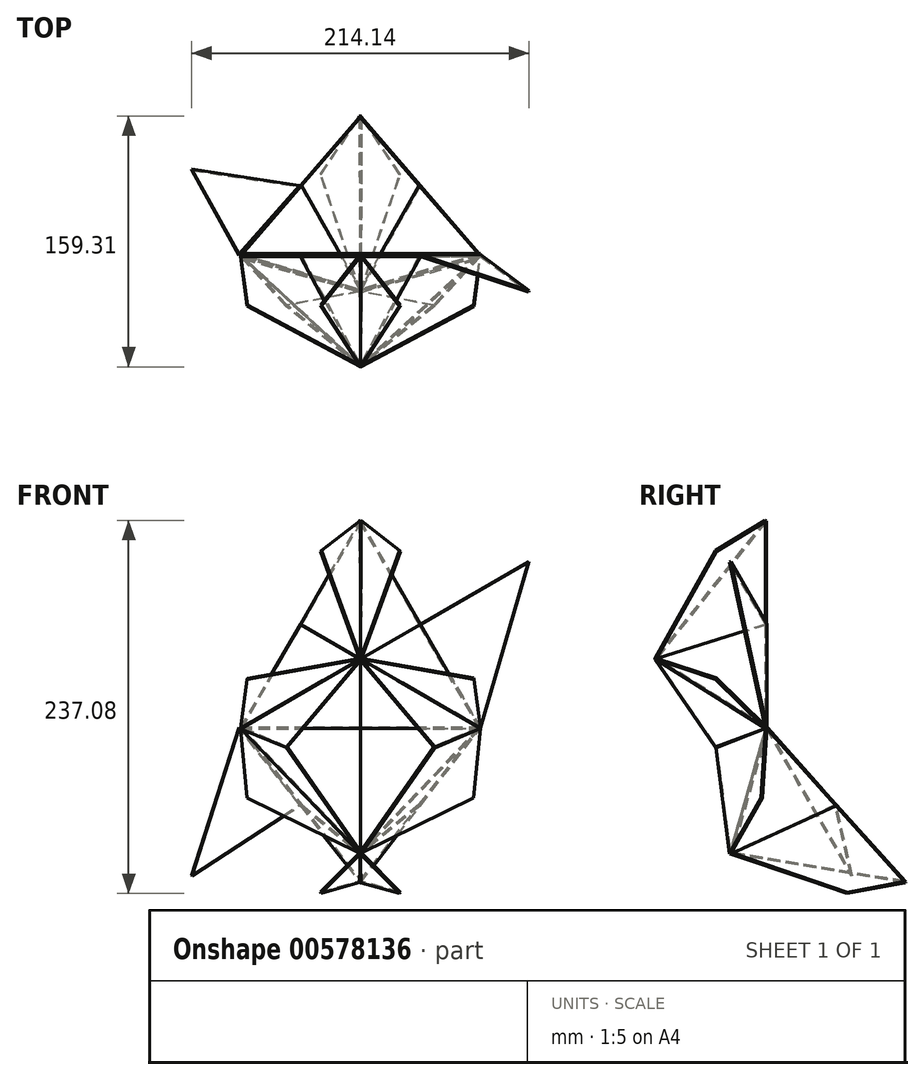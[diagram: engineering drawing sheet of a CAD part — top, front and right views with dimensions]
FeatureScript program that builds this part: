
annotation { "Feature Type Name" : "Feature", "Feature Type Description" : "" }
export const myFeature = defineFeature(function(context is Context, id is Id, definition is map)
    precondition{}
    {
        {
            var Q0;
            Q0=qCreatedBy(makeId("Front.planeOp"),FACE);
            var sketch = newSketch(context, id + "F0", { "sketchPlane" : qUnion([Q0])});
            skLineSegment(sketch, "E0", {"start": v(0, 0) * mm, "end": v(76.2, 0) * mm});
            skLineSegment(sketch, "E1", {"start": v(76.2, 0) * mm, "end": v(152.4, 0) * mm});
            skLineSegment(sketch, "E2", {"start": v(76.2, 0) * mm, "end": v(76.2, -82.55) * mm});
            skLineSegment(sketch, "E3", {"start": v(0, 0) * mm, "end": v(38.1, 66) * mm});
            skLineSegment(sketch, "E4", {"start": v(38.1, 66) * mm, "end": v(76.2, 131.98) * mm});
            skLineSegment(sketch, "E5", {"start": v(76.2, 131.98) * mm, "end": v(114.3, 66) * mm});
            skLineSegment(sketch, "E6", {"start": v(114.3, 66) * mm, "end": v(152.4, 0) * mm});
            skLineSegment(sketch, "E7", {"start": v(38.1, 66) * mm, "end": v(-33.4, 107.27) * mm});
            skLineSegment(sketch, "E8", {"start": v(114.3, 66) * mm, "end": v(185.8, 107.27) * mm});
            skLineSegment(sketch, "E9", {"start": v(0, 0) * mm, "end": v(76.2, -82.55) * mm});
            skLineSegment(sketch, "E10", {"start": v(152.4, 0) * mm, "end": v(76.2, -82.55) * mm});
            skLineSegment(sketch, "E11", {"start": v(76.2, 131.98) * mm, "end": v(185.8, 107.27) * mm});
            skLineSegment(sketch, "E12", {"start": v(152.4, 0) * mm, "end": v(185.8, 107.27) * mm});
            skLineSegment(sketch, "E13", {"start": v(76.2, 131.98) * mm, "end": v(-33.4, 107.27) * mm});
            skLineSegment(sketch, "E14", {"start": v(-33.4, 107.27) * mm, "end": v(0, 0) * mm});
            skLineSegment(sketch, "E15", {"start": v(76.2, -82.55) * mm, "end": v(3.02, -44.35) * mm});
            skLineSegment(sketch, "E16", {"start": v(3.02, -44.35) * mm, "end": v(0, 0) * mm});
            skLineSegment(sketch, "E17", {"start": v(76.2, -82.55) * mm, "end": v(149.38, -44.35) * mm});
            skLineSegment(sketch, "E18", {"start": v(149.38, -44.35) * mm, "end": v(152.4, 0) * mm});
            skLineSegment(sketch, "E19", {"start": v(152.4, 0) * mm, "end": v(189.3, 24.8) * mm});
            skLineSegment(sketch, "E20", {"start": v(189.3, 24.8) * mm, "end": v(185.8, 107.27) * mm});
            skLineSegment(sketch, "E21", {"start": v(185.8, 107.27) * mm, "end": v(116.12, 151.54) * mm});
            skLineSegment(sketch, "E22", {"start": v(116.12, 151.54) * mm, "end": v(76.2, 131.98) * mm});
            skLineSegment(sketch, "E23", {"start": v(-33.4, 107.27) * mm, "end": v(36.28, 151.54) * mm});
            skLineSegment(sketch, "E24", {"start": v(36.28, 151.54) * mm, "end": v(76.2, 131.98) * mm});
            skLineSegment(sketch, "E25", {"start": v(-33.4, 107.27) * mm, "end": v(-36.9, 24.8) * mm});
            skLineSegment(sketch, "E26", {"start": v(-36.9, 24.8) * mm, "end": v(0, 0) * mm});
            skLineSegment(sketch, "E27", {"start": v(-36.9, 24.8) * mm, "end": v(-65.66, 38.24) * mm});
            skLineSegment(sketch, "E28", {"start": v(-65.66, 38.24) * mm, "end": v(-33.4, 107.27) * mm});
            skLineSegment(sketch, "E29", {"start": v(36.28, 151.54) * mm, "end": v(10.26, 169.73) * mm});
            skLineSegment(sketch, "E30", {"start": v(10.26, 169.73) * mm, "end": v(-33.4, 107.27) * mm});
            skLineSegment(sketch, "E31", {"start": v(3.02, -44.35) * mm, "end": v(0.28, -75.98) * mm});
            skLineSegment(sketch, "E32", {"start": v(0.28, -75.98) * mm, "end": v(76.2, -82.55) * mm});
            skLineSegment(sketch, "E33", {"start": v(149.38, -44.35) * mm, "end": v(152.12, -75.98) * mm});
            skLineSegment(sketch, "E34", {"start": v(152.12, -75.98) * mm, "end": v(76.2, -82.55) * mm});
            skLineSegment(sketch, "E35", {"start": v(189.3, 24.8) * mm, "end": v(218.06, 38.24) * mm});
            skLineSegment(sketch, "E36", {"start": v(218.06, 38.24) * mm, "end": v(185.8, 107.27) * mm});
            skLineSegment(sketch, "E37", {"start": v(116.12, 151.54) * mm, "end": v(142.14, 169.73) * mm});
            skLineSegment(sketch, "E38", {"start": v(142.14, 169.73) * mm, "end": v(185.8, 107.27) * mm});
            skSolve(sketch);
        }
        {
            var Q0;
            Q0=makeQuery(id+"F0.imprint","IMPRINT",FACE,{"disambiguationData":[TD([[makeQuery(id+"F0.imprint","IMPRINT",EDGE,{"derivedFrom":sQuery(id+"F0.wireOp",EDGE,"E4")}),1.0]])]});
            var Q1;
            Q1=makeQuery(id+"F0.imprint","IMPRINT",FACE,{"disambiguationData":[TD([[makeQuery(id+"F0.imprint","IMPRINT",EDGE,{"derivedFrom":sQuery(id+"F0.wireOp",EDGE,"E0")}),-1.0]])]});
            var Q2;
            Q2=makeQuery(id+"F0.imprint","IMPRINT",FACE,{"disambiguationData":[TD([[makeQuery(id+"F0.imprint","IMPRINT",EDGE,{"derivedFrom":sQuery(id+"F0.wireOp",EDGE,"E6")}),1.0]])]});
            extrude(context, id + "F1", {"entities" : qUnion([Q0, Q1, Q2]), "depth" : 1.02 * mm, "offsetDistance" : 25.4 * mm});
        }
        {
            var Q0;
            Q0=makeQuery(id+"F1.opExtrude","SWEPT_BODY",BODY,{"disambiguationData":[OSD([sQuery(id+"F0.wireOp",EDGE,"E3"),sQuery(id+"F0.wireOp",EDGE,"E4"),sQuery(id+"F0.wireOp",EDGE,"E13"),sQuery(id+"F0.wireOp",EDGE,"E14")])]});
            var Q1;
            Q1=makeQuery(id+"F1.opExtrude","CAP_EDGE",EDGE,{"disambiguationData":[OSD([sQuery(id+"F0.wireOp",EDGE,"E3"),sQuery(id+"F0.wireOp",EDGE,"E4")])],"isStart":true});
            transform(context, id + "F2", {"entities" : qUnion([Q0]), "transformType" : TransformType.ROTATION, "transformAxis" : qUnion([Q1]), "angle" : 122 * degree, "makeCopy" : false});
        }
        {
            var Q0;
            Q0=makeQuery(id+"F1.opExtrude","SWEPT_BODY",BODY,{"disambiguationData":[OSD([sQuery(id+"F0.wireOp",EDGE,"E0"),sQuery(id+"F0.wireOp",EDGE,"E1"),sQuery(id+"F0.wireOp",EDGE,"E9"),sQuery(id+"F0.wireOp",EDGE,"E10")])]});
            var Q1;
            Q1=makeQuery(id+"F1.opExtrude","CAP_EDGE",EDGE,{"disambiguationData":[OSD([sQuery(id+"F0.wireOp",EDGE,"E0"),sQuery(id+"F0.wireOp",EDGE,"E1")])],"isStart":true});
            transform(context, id + "F3", {"entities" : qUnion([Q0]), "transformType" : TransformType.ROTATION, "transformAxis" : qUnion([Q1]), "angle" : 122 * degree, "oppositeDirection" : true, "makeCopy" : false});
        }
        {
            var Q0;
            Q0=makeQuery(id+"F1.opExtrude","SWEPT_BODY",BODY,{"disambiguationData":[OSD([sQuery(id+"F0.wireOp",EDGE,"E5"),sQuery(id+"F0.wireOp",EDGE,"E6"),sQuery(id+"F0.wireOp",EDGE,"E11"),sQuery(id+"F0.wireOp",EDGE,"E12")])]});
            var Q1;
            Q1=makeQuery(id+"F1.opExtrude","CAP_EDGE",EDGE,{"disambiguationData":[OSD([sQuery(id+"F0.wireOp",EDGE,"E5"),sQuery(id+"F0.wireOp",EDGE,"E6")])],"isStart":true});
            transform(context, id + "F4", {"entities" : qUnion([Q0]), "transformType" : TransformType.ROTATION, "transformAxis" : qUnion([Q1]), "angle" : 122 * degree, "makeCopy" : false});
        }
        {
            var Q0;
            Q0=makeQuery(id+"F0.imprint","IMPRINT",FACE,{"disambiguationData":[TD([[makeQuery(id+"F0.imprint","IMPRINT",EDGE,{"derivedFrom":sQuery(id+"F0.wireOp",EDGE,"E3")}),1.0]])]});
            var Q1;
            Q1=makeQuery(id+"F0.imprint","IMPRINT",FACE,{"disambiguationData":[TD([[makeQuery(id+"F0.imprint","IMPRINT",EDGE,{"derivedFrom":sQuery(id+"F0.wireOp",EDGE,"E1")}),-1.0]])]});
            var Q2;
            Q2=makeQuery(id+"F0.imprint","IMPRINT",FACE,{"disambiguationData":[TD([[makeQuery(id+"F0.imprint","IMPRINT",EDGE,{"derivedFrom":sQuery(id+"F0.wireOp",EDGE,"E5")}),1.0]])]});
            extrude(context, id + "F5", {"entities" : qUnion([Q0, Q1, Q2]), "depth" : 1.02 * mm, "offsetDistance" : 25.4 * mm});
        }
        {
            var Q0;
            Q0=makeQuery(id+"F5.opExtrude","SWEPT_BODY",BODY,{"disambiguationData":[OSD([sQuery(id+"F0.wireOp",EDGE,"E3"),sQuery(id+"F0.wireOp",EDGE,"E7"),sQuery(id+"F0.wireOp",EDGE,"E14")])]});
            var Q1;
            Q1=sQuery(id+"F0.wireOp",EDGE,"E3");
            transform(context, id + "F6", {"entities" : qUnion([Q0]), "transformType" : TransformType.ROTATION, "transformAxis" : qUnion([Q1]), "angle" : 122 * degree, "makeCopy" : false});
        }
        {
            var Q0;
            Q0=makeQuery(id+"F5.opExtrude","SWEPT_BODY",BODY,{"disambiguationData":[OSD([sQuery(id+"F0.wireOp",EDGE,"E1"),sQuery(id+"F0.wireOp",EDGE,"E2"),sQuery(id+"F0.wireOp",EDGE,"E10")])]});
            var Q1;
            Q1=sQuery(id+"F0.wireOp",EDGE,"E1");
            transform(context, id + "F7", {"entities" : qUnion([Q0]), "transformType" : TransformType.ROTATION, "transformAxis" : qUnion([Q1]), "angle" : 122 * degree, "oppositeDirection" : true, "makeCopy" : false});
        }
        {
            var Q0;
            Q0=makeQuery(id+"F5.opExtrude","SWEPT_BODY",BODY,{"disambiguationData":[OSD([sQuery(id+"F0.wireOp",EDGE,"E5"),sQuery(id+"F0.wireOp",EDGE,"E8"),sQuery(id+"F0.wireOp",EDGE,"E11")])]});
            var Q1;
            Q1=sQuery(id+"F0.wireOp",EDGE,"E5");
            transform(context, id + "F8", {"entities" : qUnion([Q0]), "transformType" : TransformType.ROTATION, "transformAxis" : qUnion([Q1]), "angle" : 122 * degree, "makeCopy" : false});
        }
        {
            var Q0;
            Q0=makeQuery(id+"F0.imprint","IMPRINT",FACE,{"disambiguationData":[TD([[makeQuery(id+"F0.imprint","IMPRINT",EDGE,{"derivedFrom":sQuery(id+"F0.wireOp",EDGE,"E13")}),-1.0]])]});
            var Q1;
            Q1=makeQuery(id+"F0.imprint","IMPRINT",FACE,{"disambiguationData":[TD([[makeQuery(id+"F0.imprint","IMPRINT",EDGE,{"derivedFrom":sQuery(id+"F0.wireOp",EDGE,"E14")}),-1.0]])]});
            var Q2;
            Q2=makeQuery(id+"F0.imprint","IMPRINT",FACE,{"disambiguationData":[TD([[makeQuery(id+"F0.imprint","IMPRINT",EDGE,{"derivedFrom":sQuery(id+"F0.wireOp",EDGE,"E11")}),1.0]])]});
            var Q3;
            Q3=makeQuery(id+"F0.imprint","IMPRINT",FACE,{"disambiguationData":[TD([[makeQuery(id+"F0.imprint","IMPRINT",EDGE,{"derivedFrom":sQuery(id+"F0.wireOp",EDGE,"E12")}),-1.0]])]});
            var Q4;
            Q4=makeQuery(id+"F0.imprint","IMPRINT",FACE,{"disambiguationData":[TD([[makeQuery(id+"F0.imprint","IMPRINT",EDGE,{"derivedFrom":sQuery(id+"F0.wireOp",EDGE,"E10")}),1.0]])]});
            var Q5;
            Q5=makeQuery(id+"F0.imprint","IMPRINT",FACE,{"disambiguationData":[TD([[makeQuery(id+"F0.imprint","IMPRINT",EDGE,{"derivedFrom":sQuery(id+"F0.wireOp",EDGE,"E9")}),-1.0]])]});
            extrude(context, id + "F9", {"entities" : qUnion([Q0, Q1, Q2, Q3, Q4, Q5]), "depth" : 1.02 * mm, "offsetDistance" : 25.4 * mm});
        }
        {
            var Q0;
            Q0=makeQuery(id+"F9.opExtrude","SWEPT_BODY",BODY,{"disambiguationData":[OSD([sQuery(id+"F0.wireOp",EDGE,"E14"),sQuery(id+"F0.wireOp",EDGE,"E25"),sQuery(id+"F0.wireOp",EDGE,"E26")])]});
            var Q1;
            Q1=makeQuery(id+"F9.opExtrude","SWEPT_BODY",BODY,{"disambiguationData":[OSD([sQuery(id+"F0.wireOp",EDGE,"E13"),sQuery(id+"F0.wireOp",EDGE,"E23"),sQuery(id+"F0.wireOp",EDGE,"E24")])]});
            var Q2;
            Q2=sQuery(id+"F0.wireOp",EDGE,"E3");
            transform(context, id + "F10", {"entities" : qUnion([Q0, Q1]), "transformType" : TransformType.ROTATION, "transformAxis" : qUnion([Q2]), "angle" : 122 * degree, "makeCopy" : false});
        }
        {
            var Q0;
            Q0=makeQuery(id+"F9.opExtrude","SWEPT_BODY",BODY,{"disambiguationData":[OSD([sQuery(id+"F0.wireOp",EDGE,"E9"),sQuery(id+"F0.wireOp",EDGE,"E15"),sQuery(id+"F0.wireOp",EDGE,"E16")])]});
            var Q1;
            Q1=makeQuery(id+"F9.opExtrude","SWEPT_BODY",BODY,{"disambiguationData":[OSD([sQuery(id+"F0.wireOp",EDGE,"E10"),sQuery(id+"F0.wireOp",EDGE,"E17"),sQuery(id+"F0.wireOp",EDGE,"E18")])]});
            var Q2;
            Q2=sQuery(id+"F0.wireOp",EDGE,"E1");
            transform(context, id + "F11", {"entities" : qUnion([Q0, Q1]), "transformType" : TransformType.ROTATION, "transformAxis" : qUnion([Q2]), "angle" : 122 * degree, "oppositeDirection" : true, "makeCopy" : false});
        }
        {
            var Q0;
            Q0=makeQuery(id+"F9.opExtrude","SWEPT_BODY",BODY,{"disambiguationData":[OSD([sQuery(id+"F0.wireOp",EDGE,"E12"),sQuery(id+"F0.wireOp",EDGE,"E19"),sQuery(id+"F0.wireOp",EDGE,"E20")])]});
            var Q1;
            Q1=makeQuery(id+"F9.opExtrude","SWEPT_BODY",BODY,{"disambiguationData":[OSD([sQuery(id+"F0.wireOp",EDGE,"E11"),sQuery(id+"F0.wireOp",EDGE,"E21"),sQuery(id+"F0.wireOp",EDGE,"E22")])]});
            var Q2;
            Q2=sQuery(id+"F0.wireOp",EDGE,"E6");
            transform(context, id + "F12", {"entities" : qUnion([Q0, Q1]), "transformType" : TransformType.ROTATION, "transformAxis" : qUnion([Q2]), "angle" : 122 * degree, "makeCopy" : false});
        }
        {
            var Q0;
            Q0=makeQuery(id+"F0.imprint","IMPRINT",FACE,{"disambiguationData":[TD([[makeQuery(id+"F0.imprint","IMPRINT",EDGE,{"derivedFrom":sQuery(id+"F0.wireOp",EDGE,"E6")}),1.0]])]});
            extrude(context, id + "F13", {"entities" : qUnion([Q0]), "oppositeDirection" : true, "depth" : 1.02 * mm, "offsetDistance" : 25.4 * mm});
        }
        {
            var Q0;
            Q0=makeQuery(id+"F1.opExtrude","SWEPT_BODY",BODY,{"disambiguationData":[OSD([sQuery(id+"F0.wireOp",EDGE,"E3"),sQuery(id+"F0.wireOp",EDGE,"E4"),sQuery(id+"F0.wireOp",EDGE,"E13"),sQuery(id+"F0.wireOp",EDGE,"E14")])]});
            var Q1;
            Q1=makeQuery(id+"F1.opExtrude","SWEPT_BODY",BODY,{"disambiguationData":[OSD([sQuery(id+"F0.wireOp",EDGE,"E5"),sQuery(id+"F0.wireOp",EDGE,"E6"),sQuery(id+"F0.wireOp",EDGE,"E11"),sQuery(id+"F0.wireOp",EDGE,"E12")])]});
            var Q2;
            Q2=makeQuery(id+"F1.opExtrude","SWEPT_BODY",BODY,{"disambiguationData":[OSD([sQuery(id+"F0.wireOp",EDGE,"E0"),sQuery(id+"F0.wireOp",EDGE,"E1"),sQuery(id+"F0.wireOp",EDGE,"E9"),sQuery(id+"F0.wireOp",EDGE,"E10")])]});
            var Q3;
            Q3=qCreatedBy(makeId("Top.planeOp"),FACE);
            mirror(context, id + "F14", {"entities" : qUnion([Q0, Q1, Q2]), "mirrorPlane" : qUnion([Q3])});
        }
        {
            var Q0;
            Q0=makeQuery(id+"F14.opPattern","COPY",BODY,{"derivedFrom":makeQuery(id+"F1.opExtrude","SWEPT_BODY",BODY,{"disambiguationData":[OSD([sQuery(id+"F0.wireOp",EDGE,"E0"),sQuery(id+"F0.wireOp",EDGE,"E1"),sQuery(id+"F0.wireOp",EDGE,"E9"),sQuery(id+"F0.wireOp",EDGE,"E10")])]}),"instanceName":"1"});
            var Q1;
            Q1=makeQuery(id+"F14.opPattern","COPY",BODY,{"derivedFrom":makeQuery(id+"F1.opExtrude","SWEPT_BODY",BODY,{"disambiguationData":[OSD([sQuery(id+"F0.wireOp",EDGE,"E5"),sQuery(id+"F0.wireOp",EDGE,"E6"),sQuery(id+"F0.wireOp",EDGE,"E11"),sQuery(id+"F0.wireOp",EDGE,"E12")])]}),"instanceName":"1"});
            var Q2;
            Q2=makeQuery(id+"F14.opPattern","COPY",BODY,{"derivedFrom":makeQuery(id+"F1.opExtrude","SWEPT_BODY",BODY,{"disambiguationData":[OSD([sQuery(id+"F0.wireOp",EDGE,"E3"),sQuery(id+"F0.wireOp",EDGE,"E4"),sQuery(id+"F0.wireOp",EDGE,"E13"),sQuery(id+"F0.wireOp",EDGE,"E14")])]}),"instanceName":"1"});
            var Q3;
            Q3=makeQuery(id+"F1.opExtrude","CAP_EDGE",EDGE,{"disambiguationData":[OSD([sQuery(id+"F0.wireOp",EDGE,"E0"),sQuery(id+"F0.wireOp",EDGE,"E1")])],"isStart":false});
            transform(context, id + "F15", {"entities" : qUnion([Q0, Q1, Q2]), "transformType" : TransformType.ROTATION, "transformAxis" : qUnion([Q3]), "angle" : 42 * degree, "makeCopy" : false});
        }
        {
            var Q0;
            Q0=sQuery(id+"F0.wireOp",VERTEX,"E3.start");
            var Q1;
            Q1=makeQuery(id+"F14.opPattern","COPY",VERTEX,{"derivedFrom":makeQuery(id+"F1.opExtrude","CAP_VERTEX",VERTEX,{"disambiguationData":[OSD([sQuery(id+"F0.wireOp",EDGE,"E4"),sQuery(id+"F0.wireOp",EDGE,"E5"),sQuery(id+"F0.wireOp",EDGE,"E11"),sQuery(id+"F0.wireOp",EDGE,"E13")]),OD(1.0)],"isStart":false}),"instanceName":"1"});
            var Q2;
            Q2=makeQuery(id+"F14.opPattern","COPY",VERTEX,{"derivedFrom":makeQuery(id+"F1.opExtrude","CAP_VERTEX",VERTEX,{"disambiguationData":[OSD([sQuery(id+"F0.wireOp",EDGE,"E7"),sQuery(id+"F0.wireOp",EDGE,"E13"),sQuery(id+"F0.wireOp",EDGE,"E14")])],"isStart":true}),"instanceName":"1"});
            cPlane(context, id + "F16", {"entities" : qUnion([Q0, Q1, Q2]), "cplaneType" : CPlaneType.THREE_POINT, "offset" : 25.4 * mm, "width" : 152.4 * mm, "height" : 152.4 * mm});
        }
        {
            var Q0;
            Q0=qCreatedBy(id+"F16.planeOp",FACE);
            var sketch = newSketch(context, id + "F17", { "sketchPlane" : qUnion([Q0])});
            skLineSegment(sketch, "E39", {"start": v(0, 0) * mm, "end": v(-21.92, -110.14) * mm});
            skLineSegment(sketch, "E40", {"start": v(-21.92, -110.14) * mm, "end": v(44.85, -61.6) * mm});
            skLineSegment(sketch, "E41", {"start": v(44.85, -61.6) * mm, "end": v(0, 0) * mm});
            skLineSegment(sketch, "E42", {"start": v(44.85, -61.6) * mm, "end": v(89.7, -123.2) * mm});
            skLineSegment(sketch, "E43", {"start": v(89.7, -123.2) * mm, "end": v(-21.92, -110.14) * mm});
            skSolve(sketch);
        }
        {
            var Q0;
            Q0=makeQuery(id+"F17.imprint","IMPRINT",FACE,{"disambiguationData":[TD([[makeQuery(id+"F17.imprint","IMPRINT",EDGE,{"derivedFrom":sQuery(id+"F17.wireOp",EDGE,"E39")}),1.0]])]});
            extrude(context, id + "F18", {"entities" : qUnion([Q0]), "oppositeDirection" : true, "depth" : 1.02 * mm, "offsetDistance" : 25.4 * mm});
        }
        {
            var Q0;
            Q0=makeQuery(id+"F18.opExtrude","SWEPT_BODY",BODY,{"disambiguationData":[OSD([sQuery(id+"F17.wireOp",EDGE,"E39"),sQuery(id+"F17.wireOp",EDGE,"E40"),sQuery(id+"F17.wireOp",EDGE,"E41")])]});
            var Q1;
            Q1=makeQuery(id+"F14.opPattern","COPY",EDGE,{"derivedFrom":makeQuery(id+"F1.opExtrude","CAP_EDGE",EDGE,{"disambiguationData":[OSD([sQuery(id+"F0.wireOp",EDGE,"E3"),sQuery(id+"F0.wireOp",EDGE,"E4")])],"isStart":true}),"instanceName":"1"});
            transform(context, id + "F19", {"entities" : qUnion([Q0]), "transformType" : TransformType.ROTATION, "transformAxis" : qUnion([Q1]), "angle" : 106 * degree, "makeCopy" : false});
        }
        {
            var Q0;
            Q0=makeQuery(id+"F13.opExtrude","SWEPT_BODY",BODY,{"disambiguationData":[OSD([sQuery(id+"F0.wireOp",EDGE,"E6"),sQuery(id+"F0.wireOp",EDGE,"E8"),sQuery(id+"F0.wireOp",EDGE,"E12")])]});
            var Q1;
            Q1=sQuery(id+"F0.wireOp",EDGE,"E6");
            transform(context, id + "F20", {"entities" : qUnion([Q0]), "transformType" : TransformType.ROTATION, "transformAxis" : qUnion([Q1]), "angle" : 16 * degree, "makeCopy" : false});
        }
        {
            var Q0;
            Q0=makeQuery(id+"F5.opExtrude","SWEPT_BODY",BODY,{"disambiguationData":[OSD([sQuery(id+"F0.wireOp",EDGE,"E3"),sQuery(id+"F0.wireOp",EDGE,"E7"),sQuery(id+"F0.wireOp",EDGE,"E14")])]});
            var Q1;
            Q1=makeQuery(id+"F5.opExtrude","SWEPT_BODY",BODY,{"disambiguationData":[OSD([sQuery(id+"F0.wireOp",EDGE,"E5"),sQuery(id+"F0.wireOp",EDGE,"E8"),sQuery(id+"F0.wireOp",EDGE,"E11")])]});
            var Q2;
            Q2=makeQuery(id+"F5.opExtrude","SWEPT_BODY",BODY,{"disambiguationData":[OSD([sQuery(id+"F0.wireOp",EDGE,"E1"),sQuery(id+"F0.wireOp",EDGE,"E2"),sQuery(id+"F0.wireOp",EDGE,"E10")])]});
            var Q3;
            Q3=qCreatedBy(makeId("Top.planeOp"),FACE);
            mirror(context, id + "F21", {"entities" : qUnion([Q0, Q1, Q2]), "mirrorPlane" : qUnion([Q3])});
        }
        {
            var Q0;
            Q0=makeQuery(id+"F21.opPattern","COPY",BODY,{"derivedFrom":makeQuery(id+"F5.opExtrude","SWEPT_BODY",BODY,{"disambiguationData":[OSD([sQuery(id+"F0.wireOp",EDGE,"E1"),sQuery(id+"F0.wireOp",EDGE,"E2"),sQuery(id+"F0.wireOp",EDGE,"E10")])]}),"instanceName":"1"});
            var Q1;
            Q1=makeQuery(id+"F21.opPattern","COPY",BODY,{"derivedFrom":makeQuery(id+"F5.opExtrude","SWEPT_BODY",BODY,{"disambiguationData":[OSD([sQuery(id+"F0.wireOp",EDGE,"E5"),sQuery(id+"F0.wireOp",EDGE,"E8"),sQuery(id+"F0.wireOp",EDGE,"E11")])]}),"instanceName":"1"});
            var Q2;
            Q2=makeQuery(id+"F21.opPattern","COPY",BODY,{"derivedFrom":makeQuery(id+"F5.opExtrude","SWEPT_BODY",BODY,{"disambiguationData":[OSD([sQuery(id+"F0.wireOp",EDGE,"E3"),sQuery(id+"F0.wireOp",EDGE,"E7"),sQuery(id+"F0.wireOp",EDGE,"E14")])]}),"instanceName":"1"});
            var Q3;
            Q3=makeQuery(id+"F1.opExtrude","CAP_EDGE",EDGE,{"disambiguationData":[OSD([sQuery(id+"F0.wireOp",EDGE,"E0")])],"isStart":false});
            transform(context, id + "F22", {"entities" : qUnion([Q0, Q1, Q2]), "transformType" : TransformType.ROTATION, "transformAxis" : qUnion([Q3]), "angle" : 42 * degree, "makeCopy" : false});
        }
        {
            var Q0;
            Q0=makeQuery(id+"F9.opExtrude","SWEPT_BODY",BODY,{"disambiguationData":[OSD([sQuery(id+"F0.wireOp",EDGE,"E14"),sQuery(id+"F0.wireOp",EDGE,"E25"),sQuery(id+"F0.wireOp",EDGE,"E26")])]});
            var Q1;
            Q1=makeQuery(id+"F9.opExtrude","SWEPT_BODY",BODY,{"disambiguationData":[OSD([sQuery(id+"F0.wireOp",EDGE,"E9"),sQuery(id+"F0.wireOp",EDGE,"E15"),sQuery(id+"F0.wireOp",EDGE,"E16")])]});
            var Q2;
            Q2=makeQuery(id+"F9.opExtrude","SWEPT_BODY",BODY,{"disambiguationData":[OSD([sQuery(id+"F0.wireOp",EDGE,"E11"),sQuery(id+"F0.wireOp",EDGE,"E21"),sQuery(id+"F0.wireOp",EDGE,"E22")])]});
            var Q3;
            Q3=makeQuery(id+"F9.opExtrude","SWEPT_BODY",BODY,{"disambiguationData":[OSD([sQuery(id+"F0.wireOp",EDGE,"E13"),sQuery(id+"F0.wireOp",EDGE,"E23"),sQuery(id+"F0.wireOp",EDGE,"E24")])]});
            var Q4;
            Q4=makeQuery(id+"F9.opExtrude","SWEPT_BODY",BODY,{"disambiguationData":[OSD([sQuery(id+"F0.wireOp",EDGE,"E12"),sQuery(id+"F0.wireOp",EDGE,"E19"),sQuery(id+"F0.wireOp",EDGE,"E20")])]});
            var Q5;
            Q5=makeQuery(id+"F9.opExtrude","SWEPT_BODY",BODY,{"disambiguationData":[OSD([sQuery(id+"F0.wireOp",EDGE,"E10"),sQuery(id+"F0.wireOp",EDGE,"E17"),sQuery(id+"F0.wireOp",EDGE,"E18")])]});
            var Q6;
            Q6=qCreatedBy(makeId("Top.planeOp"),FACE);
            mirror(context, id + "F23", {"entities" : qUnion([Q0, Q1, Q2, Q3, Q4, Q5]), "mirrorPlane" : qUnion([Q6])});
        }
        {
            var Q0;
            Q0=makeQuery(id+"F23.opPattern","COPY",BODY,{"derivedFrom":makeQuery(id+"F9.opExtrude","SWEPT_BODY",BODY,{"disambiguationData":[OSD([sQuery(id+"F0.wireOp",EDGE,"E14"),sQuery(id+"F0.wireOp",EDGE,"E25"),sQuery(id+"F0.wireOp",EDGE,"E26")])]}),"instanceName":"1"});
            var Q1;
            Q1=makeQuery(id+"F23.opPattern","COPY",BODY,{"derivedFrom":makeQuery(id+"F9.opExtrude","SWEPT_BODY",BODY,{"disambiguationData":[OSD([sQuery(id+"F0.wireOp",EDGE,"E12"),sQuery(id+"F0.wireOp",EDGE,"E19"),sQuery(id+"F0.wireOp",EDGE,"E20")])]}),"instanceName":"1"});
            var Q2;
            Q2=makeQuery(id+"F23.opPattern","COPY",BODY,{"derivedFrom":makeQuery(id+"F9.opExtrude","SWEPT_BODY",BODY,{"disambiguationData":[OSD([sQuery(id+"F0.wireOp",EDGE,"E10"),sQuery(id+"F0.wireOp",EDGE,"E17"),sQuery(id+"F0.wireOp",EDGE,"E18")])]}),"instanceName":"1"});
            var Q3;
            Q3=makeQuery(id+"F23.opPattern","COPY",BODY,{"derivedFrom":makeQuery(id+"F9.opExtrude","SWEPT_BODY",BODY,{"disambiguationData":[OSD([sQuery(id+"F0.wireOp",EDGE,"E9"),sQuery(id+"F0.wireOp",EDGE,"E15"),sQuery(id+"F0.wireOp",EDGE,"E16")])]}),"instanceName":"1"});
            var Q4;
            Q4=makeQuery(id+"F23.opPattern","COPY",BODY,{"derivedFrom":makeQuery(id+"F9.opExtrude","SWEPT_BODY",BODY,{"disambiguationData":[OSD([sQuery(id+"F0.wireOp",EDGE,"E11"),sQuery(id+"F0.wireOp",EDGE,"E21"),sQuery(id+"F0.wireOp",EDGE,"E22")])]}),"instanceName":"1"});
            var Q5;
            Q5=makeQuery(id+"F23.opPattern","COPY",BODY,{"derivedFrom":makeQuery(id+"F9.opExtrude","SWEPT_BODY",BODY,{"disambiguationData":[OSD([sQuery(id+"F0.wireOp",EDGE,"E13"),sQuery(id+"F0.wireOp",EDGE,"E23"),sQuery(id+"F0.wireOp",EDGE,"E24")])]}),"instanceName":"1"});
            var Q6;
            Q6=sQuery(id+"F0.wireOp",EDGE,"E1");
            transform(context, id + "F24", {"entities" : qUnion([Q0, Q1, Q2, Q3, Q4, Q5]), "transformType" : TransformType.ROTATION, "transformAxis" : qUnion([Q6]), "angle" : 42 * degree, "makeCopy" : false});
        }
        {
            var Q0;
            Q0=makeQuery(id+"F9.opExtrude","SWEPT_BODY",BODY,{"disambiguationData":[OSD([sQuery(id+"F0.wireOp",EDGE,"E12"),sQuery(id+"F0.wireOp",EDGE,"E19"),sQuery(id+"F0.wireOp",EDGE,"E20")])]});
            var Q1;
            Q1=makeQuery(id+"F5.opExtrude","CAP_EDGE",EDGE,{"disambiguationData":[OSD([sQuery(id+"F0.wireOp",EDGE,"E10")])],"isStart":true});
            transform(context, id + "F25", {"entities" : qUnion([Q0]), "transformType" : TransformType.ROTATION, "transformAxis" : qUnion([Q1]), "angle" : 20 * degree, "oppositeDirection" : true, "makeCopy" : false});
        }
        {
            var Q0;
            Q0=makeQuery(id+"F23.opPattern","COPY",BODY,{"derivedFrom":makeQuery(id+"F9.opExtrude","SWEPT_BODY",BODY,{"disambiguationData":[OSD([sQuery(id+"F0.wireOp",EDGE,"E10"),sQuery(id+"F0.wireOp",EDGE,"E17"),sQuery(id+"F0.wireOp",EDGE,"E18")])]}),"instanceName":"1"});
            var Q1;
            Q1=makeQuery(id+"F23.opPattern","COPY",BODY,{"derivedFrom":makeQuery(id+"F9.opExtrude","SWEPT_BODY",BODY,{"disambiguationData":[OSD([sQuery(id+"F0.wireOp",EDGE,"E12"),sQuery(id+"F0.wireOp",EDGE,"E19"),sQuery(id+"F0.wireOp",EDGE,"E20")])]}),"instanceName":"1"});
            var Q2;
            Q2=makeQuery(id+"F23.opPattern","COPY",EDGE,{"derivedFrom":makeQuery(id+"F9.opExtrude","CAP_EDGE",EDGE,{"disambiguationData":[OSD([sQuery(id+"F0.wireOp",EDGE,"E10")])],"isStart":true}),"instanceName":"1"});
            transform(context, id + "F26", {"entities" : qUnion([Q0, Q1]), "transformType" : TransformType.ROTATION, "transformAxis" : qUnion([Q2]), "angle" : 20 * degree, "makeCopy" : false});
        }
        {
            var Q0;
            Q0=makeQuery(id+"F9.opExtrude","SWEPT_BODY",BODY,{"disambiguationData":[OSD([sQuery(id+"F0.wireOp",EDGE,"E14"),sQuery(id+"F0.wireOp",EDGE,"E25"),sQuery(id+"F0.wireOp",EDGE,"E26")])]});
            var Q1;
            Q1=makeQuery(id+"F5.opExtrude","CAP_EDGE",EDGE,{"disambiguationData":[OSD([sQuery(id+"F0.wireOp",EDGE,"E14")])],"isStart":false});
            transform(context, id + "F27", {"entities" : qUnion([Q0]), "transformType" : TransformType.ROTATION, "transformAxis" : qUnion([Q1]), "angle" : 20 * degree, "oppositeDirection" : true, "makeCopy" : false});
        }
        {
            var Q0;
            Q0=makeQuery(id+"F23.opPattern","COPY",BODY,{"derivedFrom":makeQuery(id+"F9.opExtrude","SWEPT_BODY",BODY,{"disambiguationData":[OSD([sQuery(id+"F0.wireOp",EDGE,"E14"),sQuery(id+"F0.wireOp",EDGE,"E25"),sQuery(id+"F0.wireOp",EDGE,"E26")])]}),"instanceName":"1"});
            var Q1;
            Q1=sQuery(id+"F17.wireOp",EDGE,"E39");
            transform(context, id + "F28", {"entities" : qUnion([Q0]), "transformType" : TransformType.ROTATION, "transformAxis" : qUnion([Q1]), "angle" : 20 * degree, "oppositeDirection" : true, "makeCopy" : false});
        }
        {
            var Q0;
            Q0=makeQuery(id+"F9.opExtrude","SWEPT_BODY",BODY,{"disambiguationData":[OSD([sQuery(id+"F0.wireOp",EDGE,"E9"),sQuery(id+"F0.wireOp",EDGE,"E15"),sQuery(id+"F0.wireOp",EDGE,"E16")])]});
            var Q1;
            Q1=makeQuery(id+"F5.opExtrude","CAP_EDGE",EDGE,{"disambiguationData":[OSD([sQuery(id+"F0.wireOp",EDGE,"E14")])],"isStart":true});
            transform(context, id + "F29", {"entities" : qUnion([Q0]), "transformType" : TransformType.ROTATION, "transformAxis" : qUnion([Q1]), "angle" : 20 * degree, "makeCopy" : false});
        }
        {
            var Q0;
            Q0=makeQuery(id+"F9.opExtrude","SWEPT_BODY",BODY,{"disambiguationData":[OSD([sQuery(id+"F0.wireOp",EDGE,"E10"),sQuery(id+"F0.wireOp",EDGE,"E17"),sQuery(id+"F0.wireOp",EDGE,"E18")])]});
            var Q1;
            Q1=makeQuery(id+"F5.opExtrude","CAP_EDGE",EDGE,{"disambiguationData":[OSD([sQuery(id+"F0.wireOp",EDGE,"E10")])],"isStart":false});
            transform(context, id + "F30", {"entities" : qUnion([Q0]), "transformType" : TransformType.ROTATION, "transformAxis" : qUnion([Q1]), "angle" : 20 * degree, "makeCopy" : false});
        }
        {
            var Q0;
            Q0=makeQuery(id+"F23.opPattern","COPY",BODY,{"derivedFrom":makeQuery(id+"F9.opExtrude","SWEPT_BODY",BODY,{"disambiguationData":[OSD([sQuery(id+"F0.wireOp",EDGE,"E10"),sQuery(id+"F0.wireOp",EDGE,"E17"),sQuery(id+"F0.wireOp",EDGE,"E18")])]}),"instanceName":"1"});
            var Q1;
            Q1=makeQuery(id+"F23.opPattern","COPY",EDGE,{"derivedFrom":makeQuery(id+"F9.opExtrude","CAP_EDGE",EDGE,{"disambiguationData":[OSD([sQuery(id+"F0.wireOp",EDGE,"E12")])],"isStart":true}),"instanceName":"1"});
            transform(context, id + "F31", {"entities" : qUnion([Q0]), "transformType" : TransformType.ROTATION, "transformAxis" : qUnion([Q1]), "angle" : 20 * degree, "oppositeDirection" : true, "makeCopy" : false});
        }
        {
            var Q0;
            Q0=makeQuery(id+"F23.opPattern","COPY",BODY,{"derivedFrom":makeQuery(id+"F9.opExtrude","SWEPT_BODY",BODY,{"disambiguationData":[OSD([sQuery(id+"F0.wireOp",EDGE,"E9"),sQuery(id+"F0.wireOp",EDGE,"E15"),sQuery(id+"F0.wireOp",EDGE,"E16")])]}),"instanceName":"1"});
            var Q1;
            Q1=sQuery(id+"F17.wireOp",EDGE,"E39");
            transform(context, id + "F32", {"entities" : qUnion([Q0]), "transformType" : TransformType.ROTATION, "transformAxis" : qUnion([Q1]), "angle" : 20 * degree, "makeCopy" : false});
        }
        {
            var Q0;
            Q0=makeQuery(id+"F9.opExtrude","SWEPT_BODY",BODY,{"disambiguationData":[OSD([sQuery(id+"F0.wireOp",EDGE,"E11"),sQuery(id+"F0.wireOp",EDGE,"E21"),sQuery(id+"F0.wireOp",EDGE,"E22")])]});
            var Q1;
            Q1=makeQuery(id+"F1.opExtrude","CAP_EDGE",EDGE,{"disambiguationData":[OSD([sQuery(id+"F0.wireOp",EDGE,"E13")])],"isStart":true});
            transform(context, id + "F33", {"entities" : qUnion([Q0]), "transformType" : TransformType.ROTATION, "transformAxis" : qUnion([Q1]), "angle" : 20 * degree, "makeCopy" : false});
        }
        {
            var Q0;
            Q0=makeQuery(id+"F9.opExtrude","SWEPT_BODY",BODY,{"disambiguationData":[OSD([sQuery(id+"F0.wireOp",EDGE,"E13"),sQuery(id+"F0.wireOp",EDGE,"E23"),sQuery(id+"F0.wireOp",EDGE,"E24")])]});
            var Q1;
            Q1=makeQuery(id+"F1.opExtrude","CAP_EDGE",EDGE,{"disambiguationData":[OSD([sQuery(id+"F0.wireOp",EDGE,"E13")])],"isStart":false});
            transform(context, id + "F34", {"entities" : qUnion([Q0]), "transformType" : TransformType.ROTATION, "transformAxis" : qUnion([Q1]), "angle" : 20 * degree, "oppositeDirection" : true, "makeCopy" : false});
        }
        {
            var Q0;
            Q0=makeQuery(id+"F23.opPattern","COPY",BODY,{"derivedFrom":makeQuery(id+"F9.opExtrude","SWEPT_BODY",BODY,{"disambiguationData":[OSD([sQuery(id+"F0.wireOp",EDGE,"E11"),sQuery(id+"F0.wireOp",EDGE,"E21"),sQuery(id+"F0.wireOp",EDGE,"E22")])]}),"instanceName":"1"});
            var Q1;
            Q1=sQuery(id+"F17.wireOp",EDGE,"E43");
            transform(context, id + "F35", {"entities" : qUnion([Q0]), "transformType" : TransformType.ROTATION, "transformAxis" : qUnion([Q1]), "angle" : 20 * degree, "oppositeDirection" : true, "makeCopy" : false});
        }
        {
            var Q0;
            Q0=makeQuery(id+"F23.opPattern","COPY",BODY,{"derivedFrom":makeQuery(id+"F9.opExtrude","SWEPT_BODY",BODY,{"disambiguationData":[OSD([sQuery(id+"F0.wireOp",EDGE,"E13"),sQuery(id+"F0.wireOp",EDGE,"E23"),sQuery(id+"F0.wireOp",EDGE,"E24")])]}),"instanceName":"1"});
            var Q1;
            Q1=sQuery(id+"F17.wireOp",EDGE,"E43");
            transform(context, id + "F36", {"entities" : qUnion([Q0]), "transformType" : TransformType.ROTATION, "transformAxis" : qUnion([Q1]), "angle" : 20 * degree, "makeCopy" : false});
        }
        {
            var Q0;
            Q0=makeQuery(id+"F23.opPattern","COPY",BODY,{"derivedFrom":makeQuery(id+"F9.opExtrude","SWEPT_BODY",BODY,{"disambiguationData":[OSD([sQuery(id+"F0.wireOp",EDGE,"E10"),sQuery(id+"F0.wireOp",EDGE,"E17"),sQuery(id+"F0.wireOp",EDGE,"E18")])]}),"instanceName":"1"});
            var Q1;
            Q1=makeQuery(id+"F23.opPattern","COPY",EDGE,{"derivedFrom":makeQuery(id+"F9.opExtrude","CAP_EDGE",EDGE,{"disambiguationData":[OSD([sQuery(id+"F0.wireOp",EDGE,"E10")])],"isStart":true}),"instanceName":"1"});
            transform(context, id + "F37", {"entities" : qUnion([Q0]), "transformType" : TransformType.ROTATION, "transformAxis" : qUnion([Q1]), "angle" : 20 * degree, "oppositeDirection" : true, "makeCopy" : false});
        }
    });
